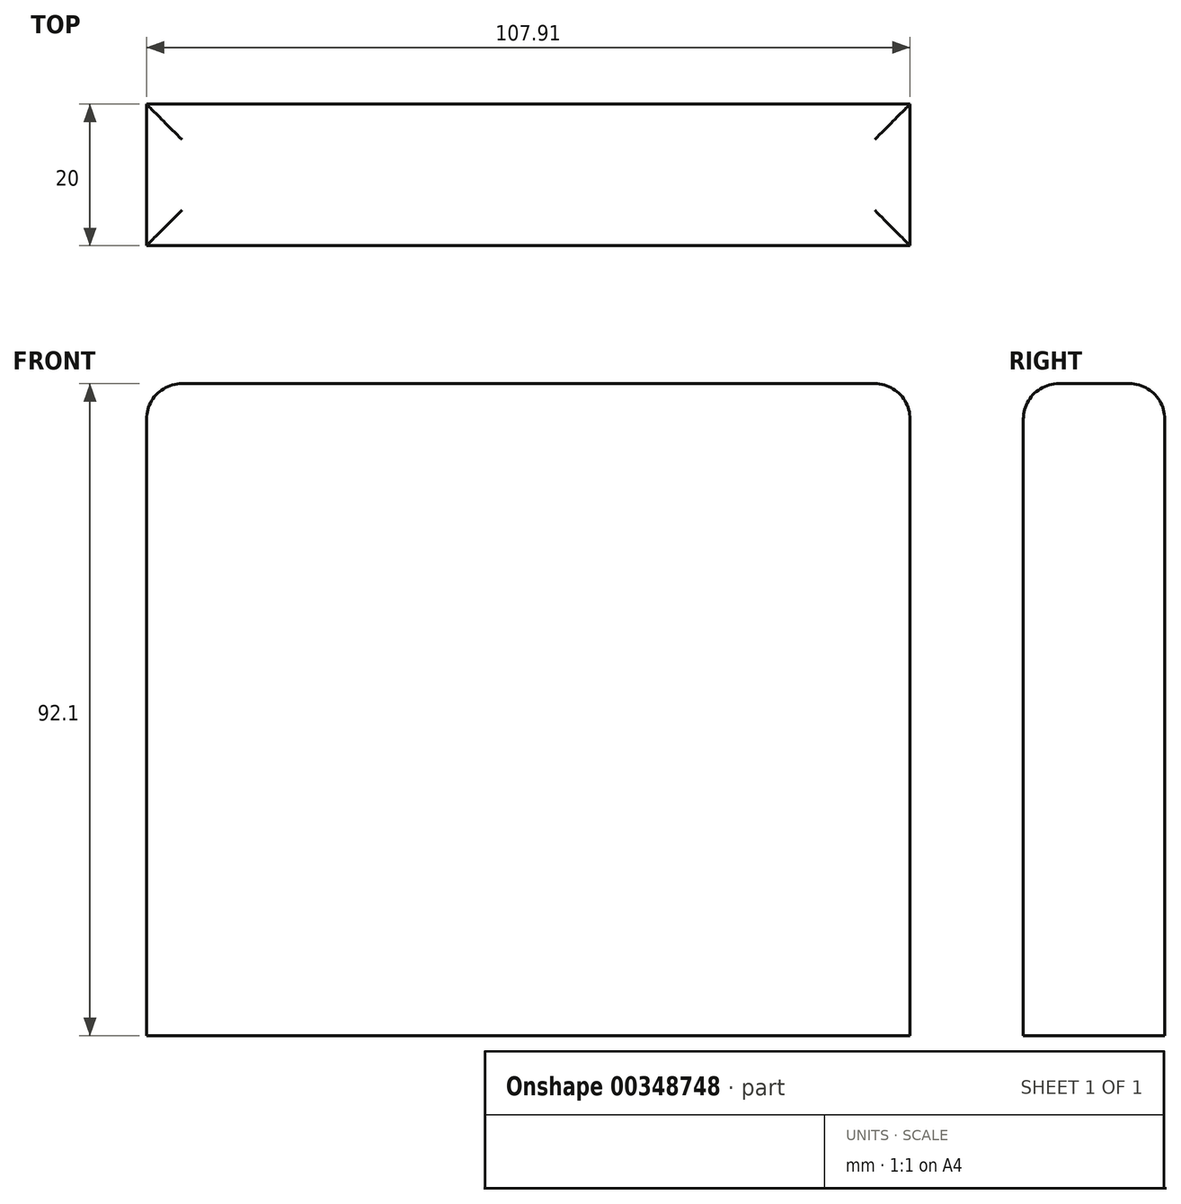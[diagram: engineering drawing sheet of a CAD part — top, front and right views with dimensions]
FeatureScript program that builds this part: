
annotation { "Feature Type Name" : "Feature", "Feature Type Description" : "" }
export const myFeature = defineFeature(function(context is Context, id is Id, definition is map)
    precondition{}
    {
        {
            var Q0;
            Q0=qCreatedBy(makeId("Front.planeOp"),FACE);
            var sketch = newSketch(context, id + "F0", { "sketchPlane" : qUnion([Q0])});
            skLineSegment(sketch, "E0.bottom", {"start": v(-60.85, 32.98) * mm, "end": v(47.06, 32.98) * mm});
            skLineSegment(sketch, "E0.top", {"start": v(-60.85, -59.12) * mm, "end": v(47.06, -59.12) * mm});
            skLineSegment(sketch, "E0.left", {"start": v(-60.85, 32.98) * mm, "end": v(-60.85, -59.12) * mm});
            skLineSegment(sketch, "E0.right", {"start": v(47.06, 32.98) * mm, "end": v(47.06, -59.12) * mm});
            skSolve(sketch);
        }
        {
            var Q0;
            Q0 = qSketchRegion(id + "F0", true);
            extrude(context, id + "F1", {"entities" : qUnion([Q0]), "depth" : 20 * mm});
        }
        {
            var Q0;
            Q0=makeQuery(id+"F1.opExtrude","SWEPT_FACE",FACE,{"disambiguationData":[OSD([sQuery(id+"F0.wireOp",EDGE,"E0.bottom")])]});
            fillet(context, id + "F2", {"entities" : qUnion([Q0]), "radius" : 5 * mm, "tangentPropagation" : true, "allowEdgeOverflow" : false});
        }
    });
